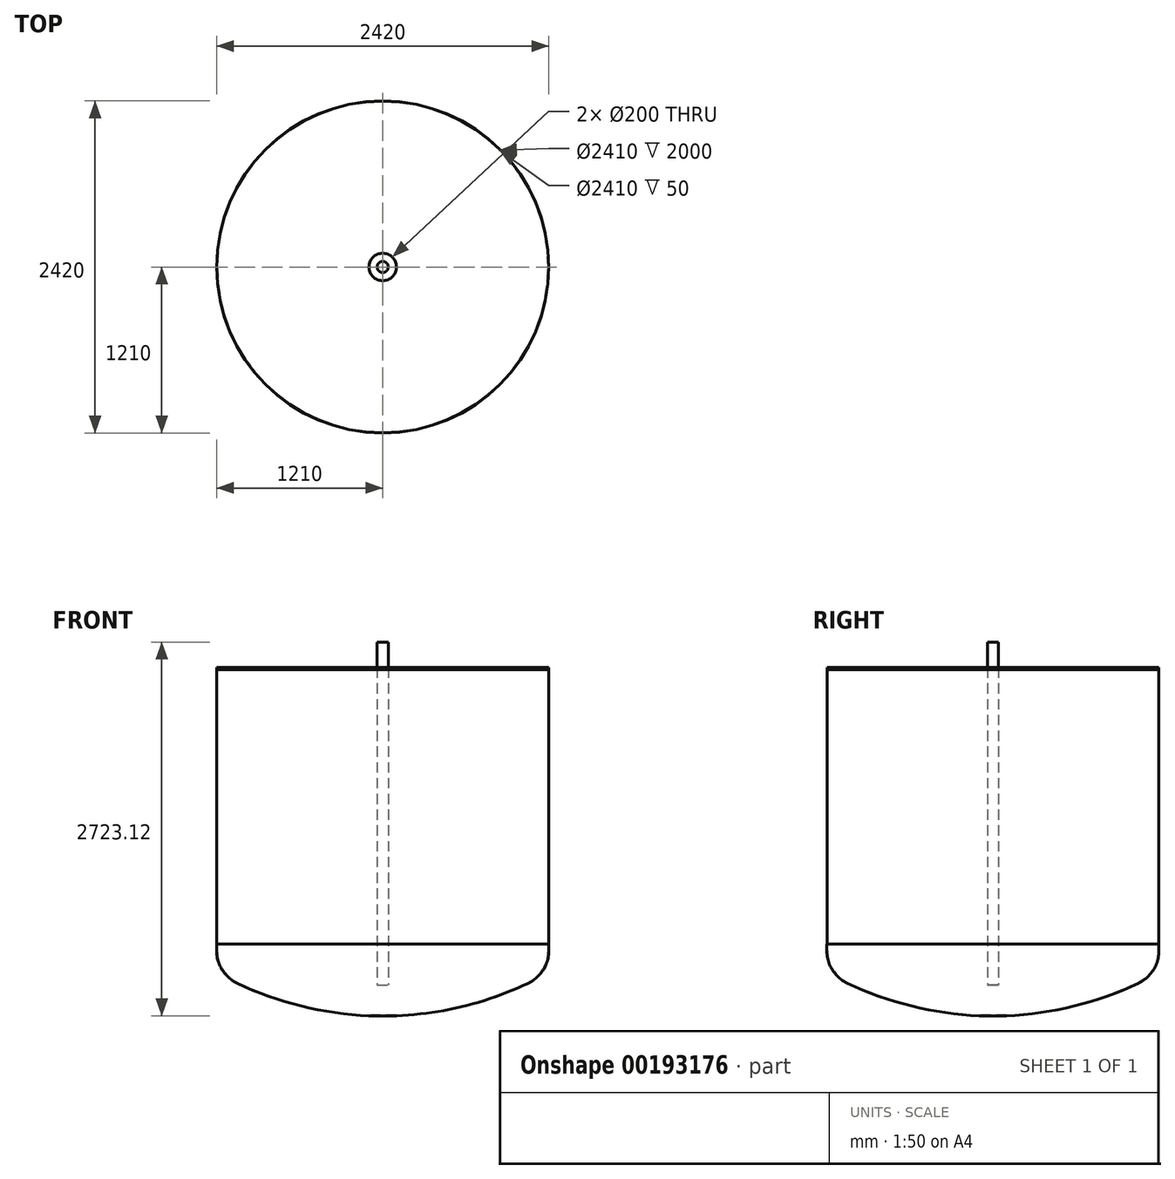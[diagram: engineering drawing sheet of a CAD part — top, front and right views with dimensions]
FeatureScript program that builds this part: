
annotation { "Feature Type Name" : "Feature", "Feature Type Description" : "" }
export const myFeature = defineFeature(function(context is Context, id is Id, definition is map)
    precondition{}
    {
        {
            var Q0;
            Q0=qCreatedBy(makeId("Front.planeOp"),FACE);
            var sketch = newSketch(context, id + "F0", { "sketchPlane" : qUnion([Q0])});
            skArc(sketch, "E0", {"start": v(0, -525.14) * mm, "mid": v(544.46, -464.26) * mm, "end": v(1062.02, -284.63) * mm});
            skArc(sketch, "E1", {"start": v(1062.02, -284.63) * mm, "mid": v(1169.91, -188.7) * mm, "end": v(1210, -50) * mm});
            skLineSegment(sketch, "E2", {"start": v(1210, -50) * mm, "end": v(1210, 0) * mm});
            skLineSegment(sketch, "E3", {"start": v(0, 21.26) * mm, "end": v(0, -42) * mm, "construction": true});
            skLineSegment(sketch, "E4", {"start": v(1210, 0) * mm, "end": v(0, 0) * mm});
            skLineSegment(sketch, "E5", {"start": v(0, 0) * mm, "end": v(0, -525.14) * mm});
            skSolve(sketch);
        }
        {
            var Q0;
            Q0=makeQuery(id+"F0.imprint","IMPRINT",FACE,{"disambiguationData":[TD([[makeQuery(id+"F0.imprint","IMPRINT",EDGE,{"derivedFrom":sQuery(id+"F0.wireOp",EDGE,"E0")}),1.0]])]});
            var Q1;
            Q1=sQuery(id+"F0.wireOp",EDGE,"E5");
            revolve(context, id + "F8", {"entities" : qUnion([Q0]), "axis" : qUnion([Q1]), "revolveType" : RevolveType.FULL});
        }
        {
            var Q0;
            Q0=makeQuery(id+"F8.opRevolve","SWEPT_FACE",FACE,{"disambiguationData":[OSD([sQuery(id+"F0.wireOp",EDGE,"E4")])]});
            shell(context, id + "F9", {"entities" : qUnion([Q0]), "thickness" : 5 * mm});
        }
        {
            var Q0;
            Q0=qCreatedBy(makeId("Front.planeOp"),FACE);
            var sketch = newSketch(context, id + "F10", { "sketchPlane" : qUnion([Q0])});
            skLineSegment(sketch, "E6", {"start": v(1205, 0) * mm, "end": v(1209, 0) * mm});
            skLineSegment(sketch, "E7", {"start": v(1209, 0) * mm, "end": v(1205, 0) * mm});
            skLineSegment(sketch, "E8", {"start": v(1205, 2000) * mm, "end": v(1205, 0) * mm});
            skLineSegment(sketch, "E9", {"start": v(1209, 0) * mm, "end": v(1209, 2000) * mm});
            skLineSegment(sketch, "E10", {"start": v(1209, 2000) * mm, "end": v(1205, 2000) * mm});
            skLineSegment(sketch, "E11", {"start": v(1205, 0) * mm, "end": v(1205, -35) * mm, "construction": true});
            skLineSegment(sketch, "E12", {"start": v(-1205, -35) * mm, "end": v(-1205, 0) * mm});
            skSolve(sketch);
        }
        {
            var Q0;
            Q0 = qSketchRegion(id + "F10", true);
            var Q1;
            Q1=sQuery(id+"F0.wireOp",EDGE,"E5");
            revolve(context, id + "F1", {"entities" : qUnion([Q0]), "axis" : qUnion([Q1]), "revolveType" : RevolveType.FULL});
        }
        {
            var Q0;
            Q0=qCreatedBy(makeId("Front.planeOp"),FACE);
            var sketch = newSketch(context, id + "F11", { "sketchPlane" : qUnion([Q0])});
            skLineSegment(sketch, "E13.0", {"start": v(0, 2000) * mm, "end": v(1209, 2000) * mm});
            skLineSegment(sketch, "E14", {"start": v(1209, 2000) * mm, "end": v(1209, 2015) * mm});
            skLineSegment(sketch, "E15", {"start": v(1209, 2015) * mm, "end": v(1209, 2015) * mm});
            skLineSegment(sketch, "E16", {"start": v(0, 2015) * mm, "end": v(1209, 2015) * mm});
            skLineSegment(sketch, "E17", {"start": v(0, 2015) * mm, "end": v(0, 2000) * mm});
            skPoint(sketch, "E18.orphan", {"position": v(-1209, 2000) * mm});
            skSolve(sketch);
        }
        {
            var Q0;
            Q0 = qSketchRegion(id + "F11", true);
            var Q1;
            Q1=sQuery(id+"F11.wireOp",EDGE,"E17");
            revolve(context, id + "F2", {"entities" : qUnion([Q0]), "axis" : qUnion([Q1]), "revolveType" : RevolveType.FULL});
        }
        {
            var Q0;
            Q0=makeQuery(id+"F2.opRevolve","SWEPT_FACE",FACE,{"disambiguationData":[OSD([sQuery(id+"F11.wireOp",EDGE,"E16")])]});
            var sketch = newSketch(context, id + "F3", { "sketchPlane" : qUnion([Q0])});
            skCircle(sketch, "E19", {"center": v(0, 0) * mm, "radius": 100 * mm});
            skSolve(sketch);
        }
        {
            var Q0;
            Q0 = qSketchRegion(id + "F3", true);
            extrude(context, id + "F4", {"entities" : qUnion([Q0]), "operationType" : NewBodyOperationType.REMOVE, "endBound" : BoundingType.THROUGH_ALL, "oppositeDirection" : true, "depth" : 25 * mm});
        }
        {
            var Q0;
            Q0=qCreatedBy(makeId("Front.planeOp"),FACE);
            var sketch = newSketch(context, id + "F5", { "sketchPlane" : qUnion([Q0])});
            skLineSegment(sketch, "E20", {"start": v(0, -2439.37) * mm, "end": v(0, 2597.25) * mm, "construction": true});
            skSolve(sketch);
        }
        {
            var Q0;
            Q0=qCreatedBy(makeId("Front.planeOp"),FACE);
            var sketch = newSketch(context, id + "F12", { "sketchPlane" : qUnion([Q0])});
            skLineSegment(sketch, "E21.bottom", {"start": v(0, 2200) * mm, "end": v(40, 2200) * mm});
            skLineSegment(sketch, "E21.top", {"start": v(0, -300) * mm, "end": v(40, -300) * mm});
            skLineSegment(sketch, "E21.left", {"start": v(0, 2200) * mm, "end": v(0, -300) * mm});
            skLineSegment(sketch, "E21.right", {"start": v(40, 2200) * mm, "end": v(40, -300) * mm});
            skSolve(sketch);
        }
        {
            var Q0;
            Q0 = qSketchRegion(id + "F12", true);
            var Q1;
            Q1=sQuery(id+"F5.wireOp",EDGE,"E20");
            revolve(context, id + "F6", {"entities" : qUnion([Q0]), "axis" : qUnion([Q1]), "revolveType" : RevolveType.FULL});
        }
    });
